# Revit family: Medical_All_Hill-Rom_Affinity-Birthing-Bed
name_source: partatom
category: Specialty Equipment
revit_build: Autodesk Revit Architecture 2015 (Build: 20140606_1530(x64)
units: mm (PartAtom-declared; Revit-internal decimal feet)

## types (1)
- Affinity® 4 Birthing Bed
    Apparent Load = 0 VA
    Assembly Code = E1020810
    BIMobject category = All
    BIMobject category code = medical-all
    BIMobject main category = Medical
    BIMobject main category code = medical
    Bed = Textile-Hill-Rom-Matress
    Brand url = https://construction.hill-rom.com
    Date of publishing = 4/2/2018
    Description = Birthing Bed
    Design country = United States
    Edition number = 1
    Frame = Plastic-Hill-Rom-Light Beige
    Frequency = 50 Hz
    Frequency Range = 50-60 Hz
    Full Load Current = 0 A
    Height = 3' - 0 21/128"
    IFC Classification = Furniture
    Installation instructions = https://construction.hill-rom.com
    Length = 7' - 6"
    Manufacturer = Hill-Rom Co.
    Manufacturer country = United States
    Manufacturer name = Hill-Rom
    Masterformat 2014 Code = 12 54 00
    Masterformat 2014 Description = Hospitality Furniture
    Mattress Length = 6' - 6"
    Mattress Section = 2' - 11 45/256"
    Mattress Weight = 13.0 lb
    Mattress Width = 2' - 11"
    Max Amperage = 2 A
    Minimum Under Bed Clearance = 0' - 3"
    Model = 4794-005
    Nominal height = 0' - 0"
    Nominal width = 0' - 0"
    OmniClass Code = 23-25 45 11 11
    OmniClass Description = Patient Beds
    Power Factor = 1
    Product Guid = f4cfdaa9-00e4-412b-8ad0-bb796970ae6f
    Product SKU = affinity-4-birthing-bed
    Product data url = https://bimobject.com
    Product family = Patient Beds
    Product group = Affinity® 4 Birthing Bed
    Product url = http://www.hill-rom.com
    QR code = http://bimobject.com
    Safe Working Load = 500 lb
    Technical description = https://construction.hill-rom.com
    Type Comments = Maternal
    UNSPSC Code = 56
    URL = www.hill-rom.com
    Uniclass 1.4 Code = L8522
    Uniclass 1.4 Description = Hospital beds
    Uniclass 2015 Code = Pr_40_50_06_39
    Uniclass 2015 Name = Hospital beds
    Voltage = 230 V
    Voltage Range = 100-230 V
    Weight Net (Kg) = 0
    Width = 3' - 3"
    Youtube clip = https://www.hill-rom.ca

## geometry (parser evidence)
native form markers: Blend x18, Sweep x2
no freeform markers — native parametric forms only
